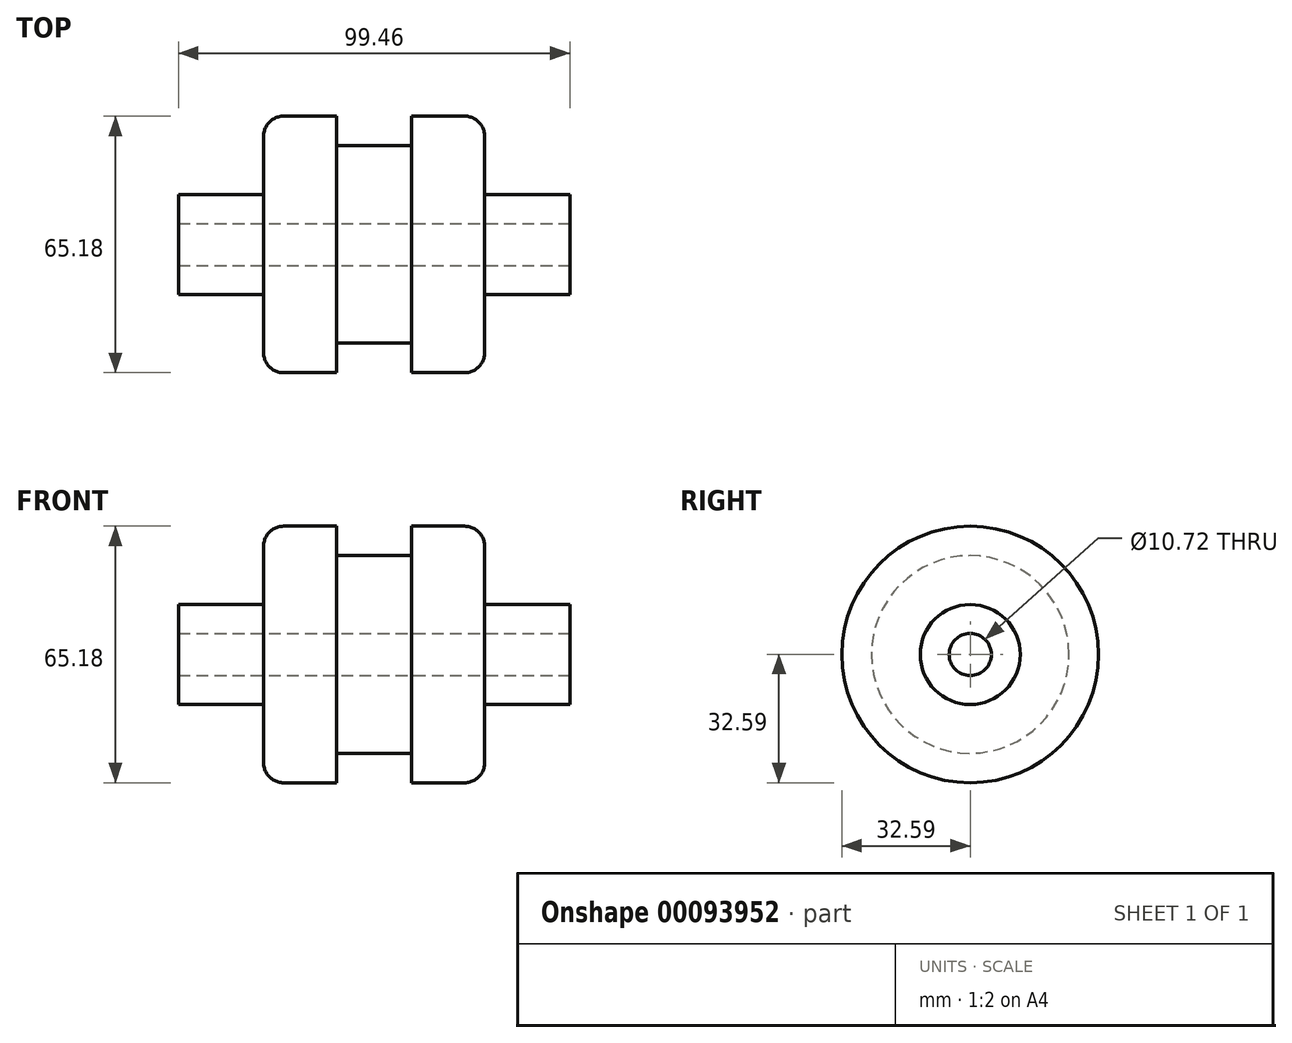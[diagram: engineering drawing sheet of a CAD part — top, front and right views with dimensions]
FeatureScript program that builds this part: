
annotation { "Feature Type Name" : "Feature", "Feature Type Description" : "" }
export const myFeature = defineFeature(function(context is Context, id is Id, definition is map)
    precondition{}
    {
        {
            var Q0;
            Q0=qCreatedBy(makeId("Front.planeOp"),FACE);
            var sketch = newSketch(context, id + "F0", { "sketchPlane" : qUnion([Q0])});
            skLineSegment(sketch, "E0", {"start": v(-49.73, 0) * mm, "end": v(-49.73, 12.7) * mm});
            skLineSegment(sketch, "E1", {"start": v(-49.73, 12.7) * mm, "end": v(-28.06, 12.7) * mm});
            skLineSegment(sketch, "E2", {"start": v(-28.06, 12.7) * mm, "end": v(-28.06, 32.6) * mm});
            skLineSegment(sketch, "E3", {"start": v(-28.06, 32.6) * mm, "end": v(28.06, 32.6) * mm});
            skLineSegment(sketch, "E4", {"start": v(28.06, 32.6) * mm, "end": v(28.06, 12.7) * mm});
            skLineSegment(sketch, "E5", {"start": v(28.06, 12.7) * mm, "end": v(49.73, 12.7) * mm});
            skLineSegment(sketch, "E6", {"start": v(49.73, 12.7) * mm, "end": v(49.73, 0) * mm});
            skLineSegment(sketch, "E7", {"start": v(49.73, 0) * mm, "end": v(-49.73, 0) * mm});
            skSolve(sketch);
        }
        {
            var Q0;
            Q0=makeQuery(id+"F0.imprint","IMPRINT",FACE,{"disambiguationData":[TD([[makeQuery(id+"F0.imprint","IMPRINT",EDGE,{"derivedFrom":sQuery(id+"F0.wireOp",EDGE,"E0")}),-1.0]])]});
            var Q1;
            Q1=sQuery(id+"F0.wireOp",EDGE,"E7");
            revolve(context, id + "F1", {"entities" : qUnion([Q0]), "axis" : qUnion([Q1]), "revolveType" : RevolveType.FULL});
        }
        {
            var Q0;
            Q0=makeQuery(id+"F1.opRevolve","SWEPT_EDGE",EDGE,{"disambiguationData":[OSD([sQuery(id+"F0.wireOp",EDGE,"E3"),sQuery(id+"F0.wireOp",EDGE,"E4")])]});
            var Q1;
            Q1=makeQuery(id+"F1.opRevolve","SWEPT_EDGE",EDGE,{"disambiguationData":[OSD([sQuery(id+"F0.wireOp",EDGE,"E2"),sQuery(id+"F0.wireOp",EDGE,"E3")])]});
            fillet(context, id + "F2", {"entities" : qUnion([Q0, Q1]), "radius" : 5.08 * mm, "tangentPropagation" : true, "allowEdgeOverflow" : false});
        }
        {
            var Q0;
            Q0=qCreatedBy(makeId("Front.planeOp"),FACE);
            var sketch = newSketch(context, id + "F3", { "sketchPlane" : qUnion([Q0])});
            skLineSegment(sketch, "E8.bottom", {"start": v(-9.52, 34.93) * mm, "end": v(9.52, 34.93) * mm});
            skLineSegment(sketch, "E8.top", {"start": v(-9.53, 25.1) * mm, "end": v(9.53, 25.1) * mm});
            skLineSegment(sketch, "E8.left", {"start": v(-9.52, 34.93) * mm, "end": v(-9.53, 25.1) * mm});
            skLineSegment(sketch, "E8.right", {"start": v(9.53, 34.93) * mm, "end": v(9.52, 25.1) * mm});
            skSolve(sketch);
        }
        {
            var Q0;
            Q0=makeQuery(id+"F3.imprint","IMPRINT",FACE,{"disambiguationData":[TD([[makeQuery(id+"F3.imprint","IMPRINT",EDGE,{"derivedFrom":sQuery(id+"F3.wireOp",EDGE,"E8.bottom")}),-1.0]])]});
            var Q1;
            Q1=makeQuery(id+"F1.opRevolve","SWEPT_FACE",FACE,{"disambiguationData":[OSD([sQuery(id+"F0.wireOp",EDGE,"E3")])]});
            revolve(context, id + "F4", {"operationType" : NewBodyOperationType.REMOVE, "entities" : qUnion([Q0]), "axis" : qUnion([Q1]), "revolveType" : RevolveType.FULL, "oppositeDirection" : true});
        }
        {
            var Q0;
            Q0=makeQuery(id+"F1.opRevolve","SWEPT_FACE",FACE,{"disambiguationData":[OSD([sQuery(id+"F0.wireOp",EDGE,"E6")])]});
            var sketch = newSketch(context, id + "F5", { "sketchPlane" : qUnion([Q0])});
            skCircle(sketch, "E9", {"center": v(0, 0) * mm, "radius": 6.35 * mm});
            skSolve(sketch);
        }
        {
            var Q0;
            Q0=sQuery(id+"F5.wireOp",VERTEX,"E9.center");
            var Q1;
            Q1=makeQuery(id+"F1.opRevolve","SWEPT_BODY",BODY,{"disambiguationData":[OSD([sQuery(id+"F0.wireOp",EDGE,"E0"),sQuery(id+"F0.wireOp",EDGE,"E1"),sQuery(id+"F0.wireOp",EDGE,"E2"),sQuery(id+"F0.wireOp",EDGE,"E3"),sQuery(id+"F0.wireOp",EDGE,"E4"),sQuery(id+"F0.wireOp",EDGE,"E5"),sQuery(id+"F0.wireOp",EDGE,"E6"),sQuery(id+"F0.wireOp",EDGE,"E7")])]});
            hole(context, id + "F6", {"style" : HoleStyle.SIMPLE, "endStyle" : HoleEndStyle.THROUGH, "standardTappedOrClearance" : lookupTablePath({ "standard" : "ANSI", "engagement" : "75%", "pitch" : "13 tpi", "size" : "1/2", "type" : "Tapped" }), "standardBlindInLast" : lookupTablePath({ "standard" : "ANSI", "engagement" : "75%", "pitch" : "13 tpi", "size" : "1/2", "type" : "Tapped" }), "holeDiameter" : 10.72 * mm, "locations" : qUnion([Q0]), "scope" : qUnion([Q1]), "isTappedThrough" : true, "majorDiameter" : 12.7 * mm, "showTappedDepth" : true});
        }
    });
